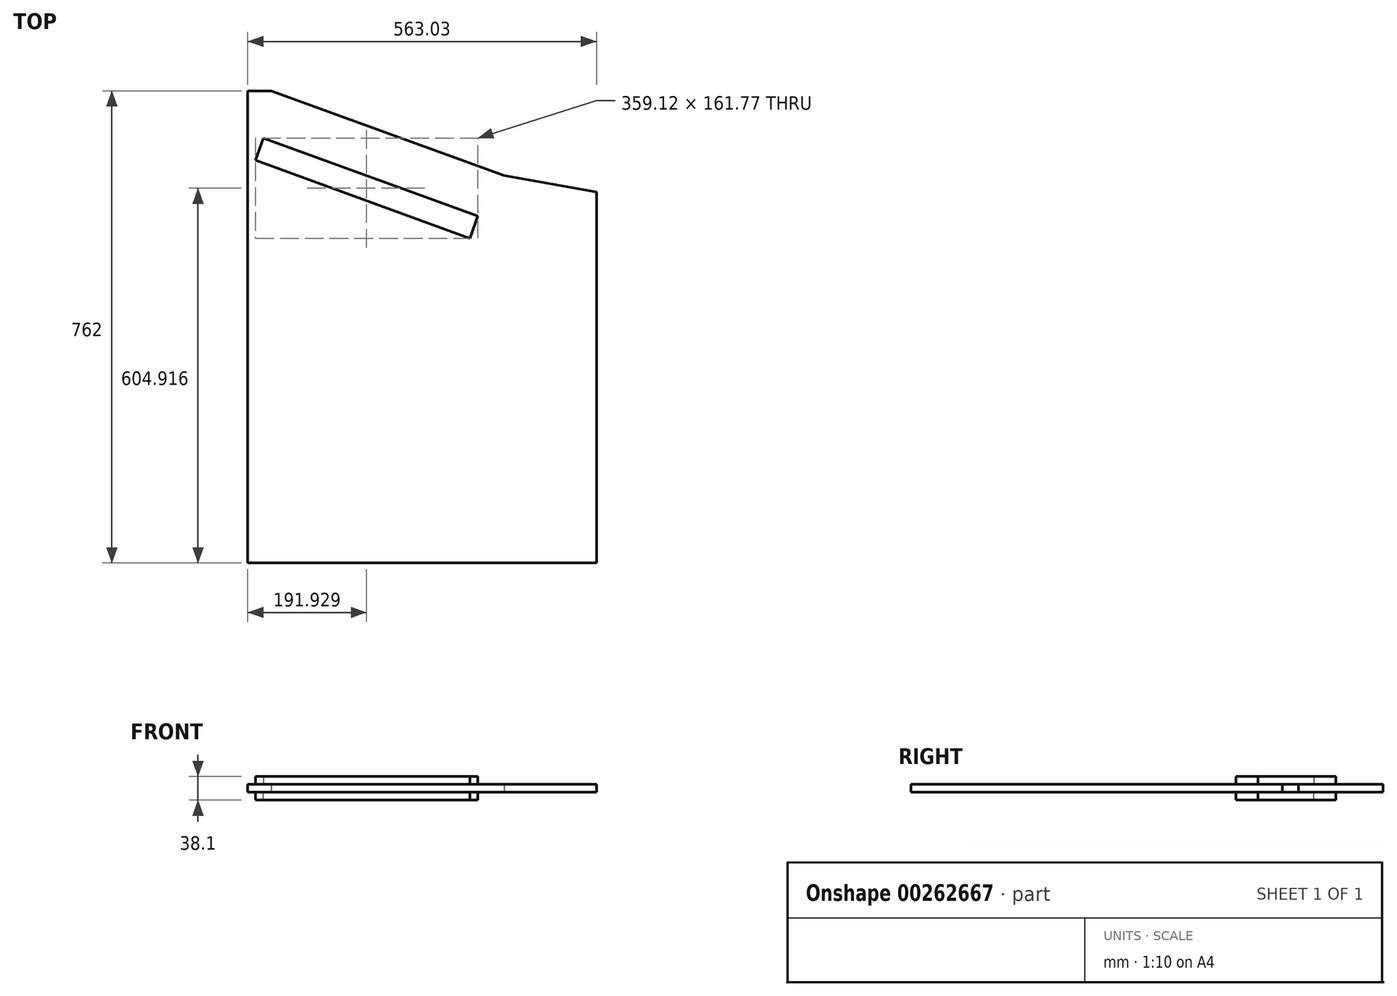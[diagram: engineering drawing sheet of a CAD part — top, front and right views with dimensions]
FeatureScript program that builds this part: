
annotation { "Feature Type Name" : "Feature", "Feature Type Description" : "" }
export const myFeature = defineFeature(function(context is Context, id is Id, definition is map)
    precondition{}
    {
        {
            var Q0;
            Q0=qCreatedBy(makeId("Top.planeOp"),FACE);
            var sketch = newSketch(context, id + "F0", { "sketchPlane" : qUnion([Q0])});
            skLineSegment(sketch, "E0.bottom", {"start": v(0, 0) * mm, "end": v(563.03, 0) * mm});
            skLineSegment(sketch, "E0.left", {"start": v(0, 0) * mm, "end": v(0, 762) * mm});
            skLineSegment(sketch, "E0.right", {"start": v(563.03, 0) * mm, "end": v(563.03, 598.92) * mm});
            skLineSegment(sketch, "E1", {"start": v(38.1, 762) * mm, "end": v(413.94, 625.2) * mm});
            skLineSegment(sketch, "E2", {"start": v(563.03, 598.92) * mm, "end": v(413.94, 625.2) * mm});
            skLineSegment(sketch, "E3", {"start": v(0, 762) * mm, "end": v(38.1, 762) * mm});
            skSolve(sketch);
        }
        {
            var Q0;
            Q0=makeQuery(id+"F0.imprint","IMPRINT",FACE,{"disambiguationData":[TD([[makeQuery(id+"F0.imprint","IMPRINT",EDGE,{"derivedFrom":sQuery(id+"F0.wireOp",EDGE,"E0.bottom")}),1.0]])]});
            extrude(context, id + "F1", {"entities" : qUnion([Q0]), "depth" : 12.7 * mm});
        }
        {
            var Q0;
            Q0=makeQuery(id+"F1.opExtrude","CAP_FACE",FACE,{"disambiguationData":[OSD([sQuery(id+"F0.wireOp",EDGE,"E0.bottom"),sQuery(id+"F0.wireOp",EDGE,"E0.left"),sQuery(id+"F0.wireOp",EDGE,"E1"),sQuery(id+"F0.wireOp",EDGE,"E0.right"),sQuery(id+"F0.wireOp",EDGE,"E2"),sQuery(id+"F0.wireOp",EDGE,"E3")])],"isStart":false});
            var sketch = newSketch(context, id + "F2", { "sketchPlane" : qUnion([Q0])});
            skLineSegment(sketch, "E4", {"start": v(25.4, 685.8) * mm, "end": v(371.49, 559.83) * mm});
            skLineSegment(sketch, "E5", {"start": v(371.49, 559.83) * mm, "end": v(358.46, 524.03) * mm});
            skLineSegment(sketch, "E6", {"start": v(358.46, 524.03) * mm, "end": v(12.37, 650) * mm});
            skLineSegment(sketch, "E7", {"start": v(12.37, 650) * mm, "end": v(25.4, 685.8) * mm});
            skSolve(sketch);
        }
        {
            var Q0;
            Q0=makeQuery(id+"F2.imprint","IMPRINT",FACE,{"disambiguationData":[TD([[makeQuery(id+"F2.imprint","IMPRINT",EDGE,{"derivedFrom":sQuery(id+"F2.wireOp",EDGE,"E4")}),-1.0]])]});
            extrude(context, id + "F3", {"entities" : qUnion([Q0]), "operationType" : NewBodyOperationType.ADD, "depth" : 12.7 * mm, "offsetDistance" : 25.4 * mm});
        }
        {
            var Q0;
            Q0=makeQuery(id+"F1.opExtrude","CAP_FACE",FACE,{"disambiguationData":[OSD([sQuery(id+"F0.wireOp",EDGE,"E0.bottom"),sQuery(id+"F0.wireOp",EDGE,"E0.left"),sQuery(id+"F0.wireOp",EDGE,"E1"),sQuery(id+"F0.wireOp",EDGE,"E0.right"),sQuery(id+"F0.wireOp",EDGE,"E2"),sQuery(id+"F0.wireOp",EDGE,"E3")])],"isStart":true});
            var sketch = newSketch(context, id + "F4", { "sketchPlane" : qUnion([Q0])});
            skLineSegment(sketch, "E8.0.0", {"start": v(413.94, -625.2) * mm, "end": v(38.1, -762) * mm, "construction": true});
            skLineSegment(sketch, "E8.0.1", {"start": v(38.1, -762) * mm, "end": v(0, -762) * mm, "construction": true});
            skLineSegment(sketch, "E8.0.2", {"start": v(0, -762) * mm, "end": v(0, 0) * mm, "construction": true});
            skLineSegment(sketch, "E8.0.3", {"start": v(0, 0) * mm, "end": v(563.03, 0) * mm, "construction": true});
            skLineSegment(sketch, "E8.0.4", {"start": v(563.03, 0) * mm, "end": v(563.03, -598.92) * mm, "construction": true});
            skLineSegment(sketch, "E8.0.5", {"start": v(563.03, -598.92) * mm, "end": v(413.94, -625.2) * mm, "construction": true});
            skLineSegment(sketch, "E9.0", {"start": v(25.4, -685.8) * mm, "end": v(371.49, -559.83) * mm});
            skLineSegment(sketch, "E10.0", {"start": v(371.49, -559.83) * mm, "end": v(358.46, -524.03) * mm});
            skLineSegment(sketch, "E11.0", {"start": v(358.46, -524.03) * mm, "end": v(12.37, -650) * mm});
            skLineSegment(sketch, "E12.0", {"start": v(12.37, -650) * mm, "end": v(25.4, -685.8) * mm});
            skSolve(sketch);
        }
        {
            var Q0;
            Q0=makeQuery(id+"F4.imprint","IMPRINT",FACE,{"disambiguationData":[TD([[makeQuery(id+"F4.imprint","IMPRINT",EDGE,{"derivedFrom":sQuery(id+"F4.wireOp",EDGE,"E9.0")}),1.0]])]});
            extrude(context, id + "F5", {"entities" : qUnion([Q0]), "operationType" : NewBodyOperationType.ADD, "depth" : 12.7 * mm, "offsetDistance" : 25.4 * mm});
        }
    });
